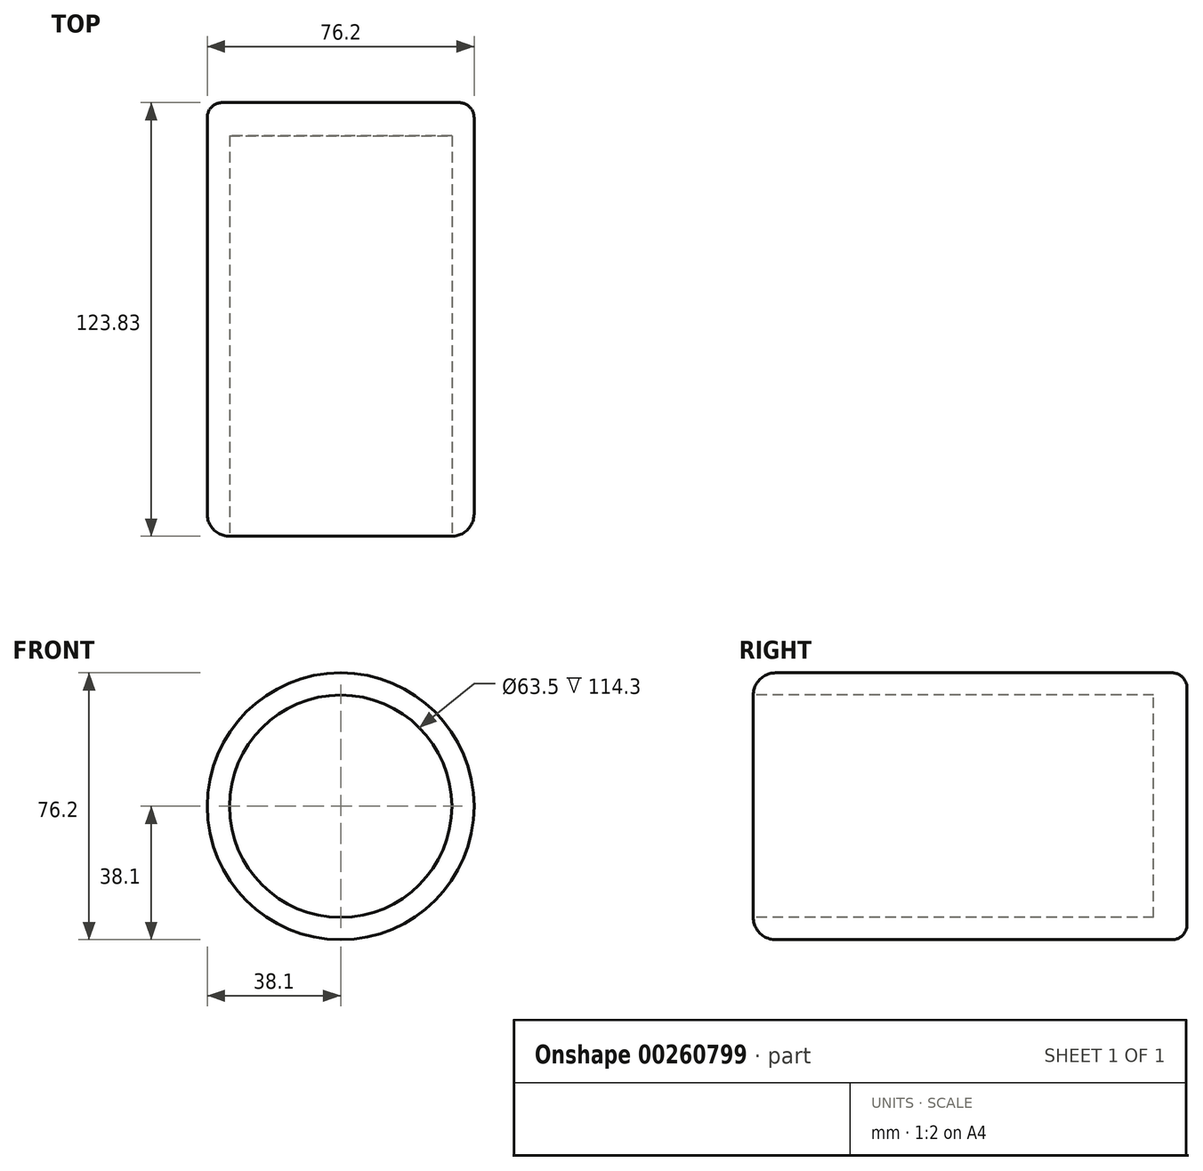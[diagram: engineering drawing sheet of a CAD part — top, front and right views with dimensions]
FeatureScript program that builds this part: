
annotation { "Feature Type Name" : "Feature", "Feature Type Description" : "" }
export const myFeature = defineFeature(function(context is Context, id is Id, definition is map)
    precondition{}
    {
        {
            var Q0;
            Q0=qCreatedBy(makeId("Front.planeOp"),FACE);
            var sketch = newSketch(context, id + "F0", { "sketchPlane" : qUnion([Q0])});
            skCircle(sketch, "E0", {"center": v(0, 0) * mm, "radius": 38.1 * mm});
            skSolve(sketch);
        }
        {
            var Q0;
            Q0 = qSketchRegion(id + "F0", true);
            extrude(context, id + "F1", {"entities" : qUnion([Q0]), "depth" : 123.82 * mm});
        }
        {
            var Q0;
            Q0=makeQuery(id+"F1.opExtrude","CAP_EDGE",EDGE,{"disambiguationData":[OSD([sQuery(id+"F0.wireOp",EDGE,"E0")])],"isStart":false});
            fillet(context, id + "F2", {"entities" : qUnion([Q0]), "radius" : 6.35 * mm, "tangentPropagation" : true, "allowEdgeOverflow" : false});
        }
        {
            var Q0;
            Q0=makeQuery(id+"F1.opExtrude","CAP_FACE",FACE,{"disambiguationData":[OSD([sQuery(id+"F0.wireOp",EDGE,"E0")])],"isStart":false});
            extrude(context, id + "F3", {"entities" : qUnion([Q0]), "operationType" : NewBodyOperationType.REMOVE, "oppositeDirection" : true, "depth" : 114.3 * mm});
        }
        {
            var Q0;
            Q0=makeQuery(id+"F1.opExtrude","CAP_EDGE",EDGE,{"disambiguationData":[OSD([sQuery(id+"F0.wireOp",EDGE,"E0")])],"isStart":true});
            fillet(context, id + "F4", {"entities" : qUnion([Q0]), "radius" : 4.3 * mm, "tangentPropagation" : true, "allowEdgeOverflow" : false});
        }
    });
